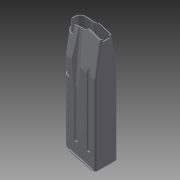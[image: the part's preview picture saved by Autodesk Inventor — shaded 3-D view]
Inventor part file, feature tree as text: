
AUTODESK INVENTOR PART (.ipt)
format: ipt  version: 2014 SP2 (Build 180246200, 246)  size: 2,461,696 bytes
history: native  units: in
note: dims shown in document units (in); Inventor stores cm internally (conversion verified against a paired STEP export)
features: sketch x24, fillet x18, projected_geometry x18, extrude x16, plane x7, chamfer x6, emboss x5, other x4, mirror x3, revolve x2, shell x1
ambient origin geometry x8: Origin, YZ Plane, XZ Plane, XY Plane, X Axis, Y Axis, Z Axis, Center Point
bodies: Solid1 (feature_tree)
feature tree (104):
  extrude  "Extrusion1"  Depth=0.855in
  extrude  "Extrusion2"  TaperAngle=75.0deg  [1 undecoded]
  extrude  "Extrusion6"  Depth=2.107in TaperAngle=0.0deg
  plane  "Work Plane3"
  sketch  "Sketch9"  dims[d29=4.214in d30=0.0in d31=90.0deg d32=3.05in d33=0.0687in]
  extrude  "Extrusion7"  TaperAngle=90.0deg  [1 undecoded]
  fillet  "Fillet5"  Radius=3.05in
  fillet  "Fillet6"  Radius=0.0687in
  extrude  "Extrusion19"  Depth=0.0625in
  sketch  "Sketch12"  dims[d38=0.2188in d39=4.0465in]
  plane  "Work Plane14"
  extrude  "Extrusion20"  Depth=4.0465in
  mirror  "Mirror4"
  plane  "Work Plane4"
  sketch  "Sketch15"  dims[d44=0.375in d45=0.375in]
  other  "Work Point1"
  extrude  "Extrusion10"  Depth=0.2656in
  plane  "Work Plane5"
  other  "Work Point2"
  other  "Work Point4"
  other  "Work Point5"
  extrude  "Extrusion11"  Depth=0.375in
  plane  "Work Plane6"
  plane  "Work Plane7"
  sketch  "Sketch22"  dims[d52=0.5in d53=0.0325in]
  revolve  "Revolution2"  [1 undecoded]
  revolve  "Revolution3"  [1 undecoded]
  extrude  "Extrusion12"  [1 undecoded]
  mirror  "Mirror2"
  plane  "Work Plane13"
  extrude  "Extrusion17"  Depth=0.031in
  shell  "Shell1"  Thickness=0.2727in
  fillet  "Fillet24"  Radius=0.2727in
  fillet  "Fillet25"  Radius=1.0in
  fillet  "Fillet26"  Radius=0.031in
  fillet  "Fillet39"  Radius=3.6685in
  fillet  "Fillet40"  Radius=1.0in
  fillet  "Fillet41"  Radius=0.183in
  fillet  "Fillet42"  Radius=1.0012in
  fillet  "Fillet29"  Radius=1.0in
  fillet  "Fillet30"  Radius=0.115in
  extrude  "Extrusion13"  Depth=1.0in TaperAngle=0.0deg
  extrude  "Extrusion14"  Depth=0.3955in
  extrude  "Extrusion15"  Depth=0.829in
  extrude  "Extrusion16"  Depth=1.0in TaperAngle=0.0deg
  emboss  "Emboss1"
  sketch  "Sketch35"  dims[d130=3.2685in d131=0.75in d132=0.0in d134=0.8895in d135=0.001in d136=0.0in d137=0.335in d138=0.6558in d139=0.368in d140=0.001in d141=0.0in d142=0.001in d143=0.0in d144=0.001in d145=0.0in]
  emboss  "Emboss2"
  emboss  "Emboss3"
  emboss  "Emboss4"
  extrude  "Extrusion18"  Depth=0.2185in
  mirror  "Mirror3"
  chamfer  "Chamfer2"  Distance=0.75in
  fillet  "Fillet31"  Radius=0.8895in
  fillet  "Fillet33"  Radius=0.001in
  fillet  "Fillet34"  Radius=0.335in
  fillet  "Fillet35"  Radius=0.6558in
  fillet  "Fillet36"  Radius=0.368in
  fillet  "Fillet37"  Radius=0.001in
  fillet  "Fillet38"  Radius=0.001in
  chamfer  "Chamfer3"  Distance=0.001in
  chamfer  "Chamfer4"  Distance=0.045in
  chamfer  "Chamfer5"  Distance=0.5in
  chamfer  "Chamfer6"  Distance=0.02in
  emboss  "Emboss5"
  chamfer  "Chamfer7"  Distance=0.05in
  extrude  "Extrusion21"  Depth=0.031in
  sketch  "Sketch1"  dims[d0=1.264in d1=0.855in]
  sketch  "Sketch2"  dims[d4=4.214in d5=0.0in d7=75.0deg]
  sketch  "Sketch8"  dims[d8=4.214in d9=0.0in d26=2.107in d27=0.0in]
  projected_geometry  "Projected Loop3"
  projected_geometry  "Projected Loop4"
  sketch  "Sketch11"  dims[d34=4.214in d35=0.0in d37=0.0625in]
  sketch  "Sketch14"  dims[d40=0.502in d41=0.2656in]
  projected_geometry  "Projected Loop5"
  sketch  "Sketch17"  dims[d47=0.38in d50=-0.314in]
  projected_geometry  "Projected Loop10"
  projected_geometry  "Projected Loop11"
  projected_geometry  "Projected Loop14"
  sketch  "Sketch28"  dims[d54=0.1in d55=0.0in d57=-0.567in]
  projected_geometry  "Projected Loop15"
  sketch  "Sketch29"  dims[d61=0.1in d62=0.0in d68=0.5in d69=0.2727in d70=0.2727in d100=1.0in d101=0.0in d105=0.031in d107=3.6685in d108=1.0in d109=0.0in d110=0.183in d112=1.0012in d114=1.0in d115=0.0in d116=0.115in]
  sketch  "Sketch30"  dims[d117=0.491in d119=1.0in d120=0.0in]
  sketch  "Sketch31"  dims[d121=0.1205in d122=0.3955in]
  sketch  "Sketch32"  dims[d123=0.871in d124=0.829in]
  sketch  "Sketch33"  dims[d125=0.85in d126=1.0in d127=0.0in]
  sketch  "Sketch34"  dims[d128=-2.375in d129=0.2185in]
  sketch  "Sketch36"  dims[d146=0.03in]
  sketch  "Sketch40"  dims[d147=0.95in d148=0.045in d149=0.0in]
  projected_geometry  "Projected Loop20"
  sketch  "Sketch41"  dims[d160=0.3436in]
  projected_geometry  "Projected Loop21"
  projected_geometry  "Projected Loop23"
  sketch  "Sketch44"  dims[d161=0.3436in]
  sketch  "Sketch45"  dims[d168=0.3625in]
  sketch  "Sketch46"  dims[d169=0.02in d170=0.5in d173=0.02in d174=0.05in d175=0.248in d176=0.05in d177=0.125in d178=45.0deg d179=0.02in d181=0.325in d182=0.02in d183=0.02in d184=0.02in d185=0.5in d186=0.02in d187=0.02in d188=0.045in d189=45.0deg d190=0.02in d191=0.045in d192=45.0deg d193=0.045in d194=0.02in d195=45.0deg d196=0.045in d197=0.02in d198=45.0deg d200=0.375in d202=0.421in d203=4.2185in d204=0.4947in d205=4.163in d206=0.0687in d207=0.031in d208=1.0in d209=0.0in d210=0.375in d211=0.076in d212=1.0in d213=0.0in d214=1.497in d215=0.09in d216=0.1801in d217=0.1801in d218=0.001in d219=0.0in d220=0.6528in d222=0.031in d223=0.375in d225=0.031in d226=0.02in d227=0.01in d228=0.02in d229=0.01in d230=0.05in d231=0.125in d232=45.0deg d233=1.0in d234=0.0in]
  projected_geometry  "Projected Loop24"
  projected_geometry  "Project Cut Edges1"
  projected_geometry  "Project Cut Edges2"
  projected_geometry  "Project Cut Edges3"
  projected_geometry  "Project Cut Edges4"
  projected_geometry  "Project Cut Edges8"
  projected_geometry  "Project Cut Edges9"
  projected_geometry  "Project Cut Edges11"
note: 5 required parameter values undecoded (feature->parameter linkage not recoverable at this tier; creation-order binding heuristic only, values carry confidence <= 0.55)